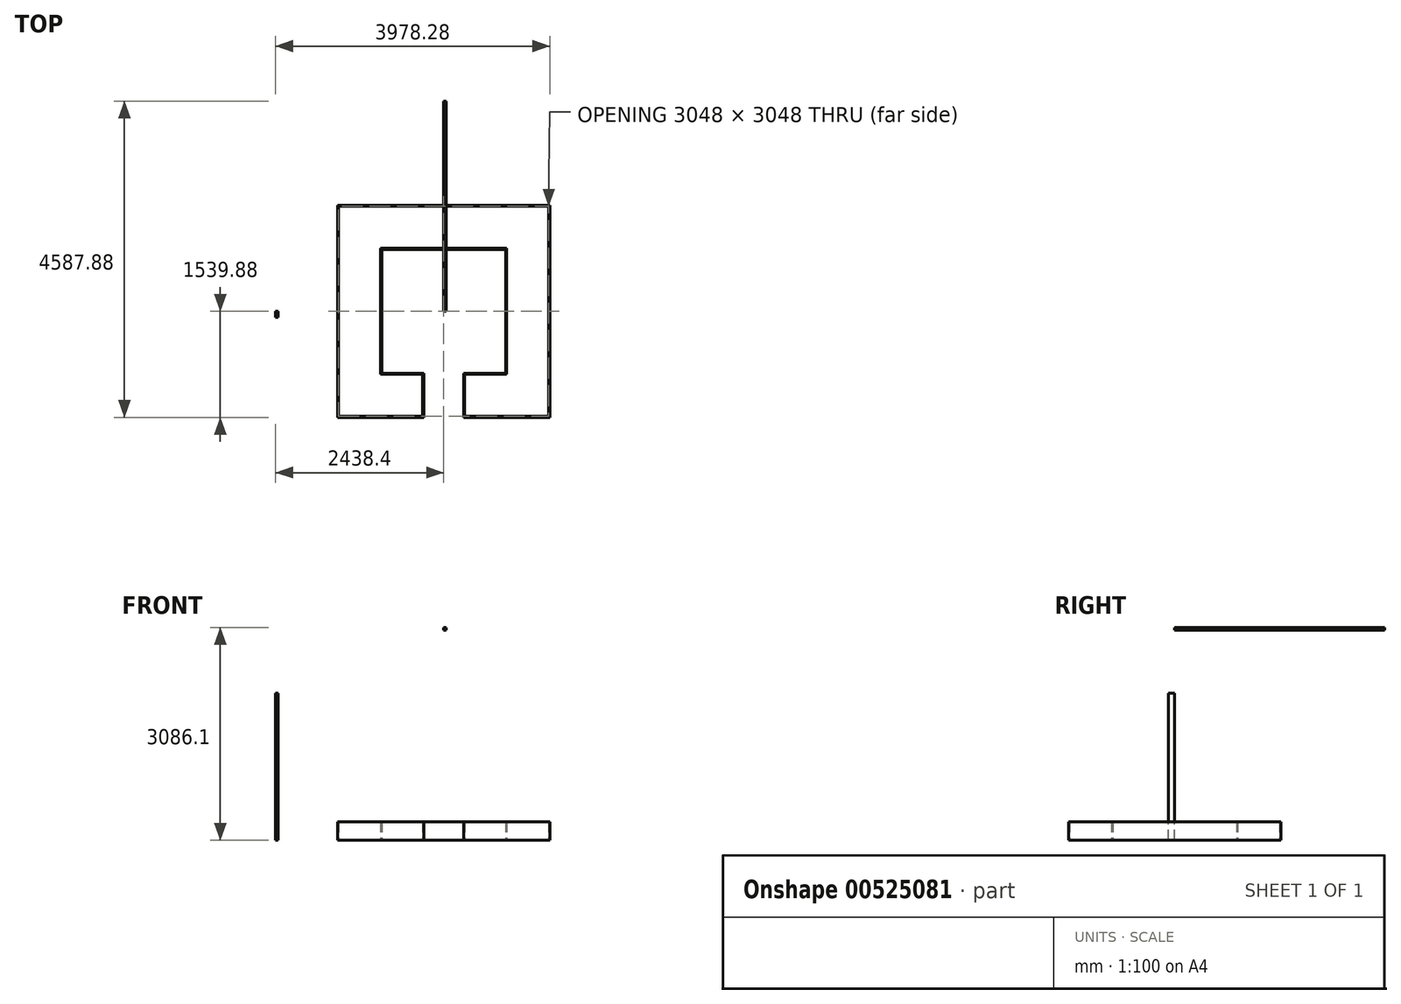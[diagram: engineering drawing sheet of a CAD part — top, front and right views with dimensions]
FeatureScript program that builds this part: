
annotation { "Feature Type Name" : "Feature", "Feature Type Description" : "" }
export const myFeature = defineFeature(function(context is Context, id is Id, definition is map)
    precondition{}
    {
        {
            var Q0;
            Q0=qCreatedBy(makeId("Top.planeOp"),FACE);
            var sketch = newSketch(context, id + "F0", { "sketchPlane" : qUnion([Q0])});
            skLineSegment(sketch, "E0.bottom", {"start": v(1524, -1524) * mm, "end": v(304.8, -1524) * mm});
            skLineSegment(sketch, "E0.top", {"start": v(1524, 1524) * mm, "end": v(-1524, 1524) * mm});
            skLineSegment(sketch, "E0.left", {"start": v(1524, -1524) * mm, "end": v(1524, 1524) * mm});
            skLineSegment(sketch, "E0.right", {"start": v(-1524, -1524) * mm, "end": v(-1524, 1524) * mm});
            skPoint(sketch, "E0.middle", {"position": v(0, 0) * mm});
            skLineSegment(sketch, "E1.bottom", {"start": v(1539.88, -1539.88) * mm, "end": v(288.93, -1539.88) * mm});
            skLineSegment(sketch, "E1.top", {"start": v(1539.88, 1539.88) * mm, "end": v(-1539.88, 1539.88) * mm});
            skLineSegment(sketch, "E1.left", {"start": v(1539.88, -1539.88) * mm, "end": v(1539.88, 1539.88) * mm});
            skLineSegment(sketch, "E1.right", {"start": v(-1539.88, -1539.88) * mm, "end": v(-1539.88, 1539.88) * mm});
            skLineSegment(sketch, "E2.bottom", {"start": v(914.4, -914.4) * mm, "end": v(304.8, -914.4) * mm});
            skLineSegment(sketch, "E2.top", {"start": v(914.4, 914.4) * mm, "end": v(-914.4, 914.4) * mm});
            skLineSegment(sketch, "E2.left", {"start": v(914.4, -914.4) * mm, "end": v(914.4, 914.4) * mm});
            skLineSegment(sketch, "E2.right", {"start": v(-914.4, -914.4) * mm, "end": v(-914.4, 914.4) * mm});
            skLineSegment(sketch, "E3.bottom", {"start": v(898.52, -898.52) * mm, "end": v(288.93, -898.52) * mm});
            skLineSegment(sketch, "E3.top", {"start": v(898.52, 898.52) * mm, "end": v(-898.52, 898.52) * mm});
            skLineSegment(sketch, "E3.left", {"start": v(898.52, -898.52) * mm, "end": v(898.52, 898.52) * mm});
            skLineSegment(sketch, "E3.right", {"start": v(-898.52, -898.52) * mm, "end": v(-898.52, 898.52) * mm});
            skLineSegment(sketch, "E4", {"start": v(288.93, -898.52) * mm, "end": v(288.93, -1539.88) * mm});
            skLineSegment(sketch, "E5", {"start": v(-288.93, -898.52) * mm, "end": v(-288.93, -1539.88) * mm});
            skLineSegment(sketch, "E6", {"start": v(304.8, -914.4) * mm, "end": v(304.8, -1524) * mm});
            skLineSegment(sketch, "E7", {"start": v(-304.8, -914.4) * mm, "end": v(-304.8, -1524) * mm});
            skLineSegment(sketch, "E8.trimOffspring", {"start": v(-288.93, -898.52) * mm, "end": v(-898.52, -898.52) * mm});
            skLineSegment(sketch, "E9.trimOffspring", {"start": v(-304.8, -914.4) * mm, "end": v(-914.4, -914.4) * mm});
            skLineSegment(sketch, "E10.trimOffspring", {"start": v(-288.93, -1539.88) * mm, "end": v(-1539.88, -1539.88) * mm});
            skLineSegment(sketch, "E11.trimOffspring", {"start": v(-304.8, -1524) * mm, "end": v(-1524, -1524) * mm});
            skSolve(sketch);
        }
        {
            var Q0;
            Q0 = qSketchRegion(id + "F0", true);
            extrude(context, id + "F1", {"entities" : qUnion([Q0]), "depth" : 266.7 * mm, "offsetDistance" : 30.48 * mm});
        }
        {
            var Q0;
            Q0=qCreatedBy(makeId("Right.planeOp"),FACE);
            cPlane(context, id + "F2", {"entities" : qUnion([Q0]), "cplaneType" : CPlaneType.OFFSET, "offset" : 2438.4 * mm, "oppositeDirection" : true, "width" : 152.4 * mm, "height" : 152.4 * mm});
        }
        {
            var Q0;
            Q0=qCreatedBy(id+"F2.planeOp",FACE);
            var sketch = newSketch(context, id + "F3", { "sketchPlane" : qUnion([Q0])});
            skLineSegment(sketch, "E12.bottom", {"start": v(0, 0) * mm, "end": v(-88.9, 0) * mm});
            skLineSegment(sketch, "E12.top", {"start": v(0, 2133.6) * mm, "end": v(-88.9, 2133.6) * mm});
            skLineSegment(sketch, "E12.left", {"start": v(0, 0) * mm, "end": v(0, 2133.6) * mm});
            skLineSegment(sketch, "E12.right", {"start": v(-88.9, 0) * mm, "end": v(-88.9, 2133.6) * mm});
            skSolve(sketch);
        }
        {
            var Q0;
            Q0 = qSketchRegion(id + "F3", true);
            extrude(context, id + "F4", {"entities" : qUnion([Q0]), "depth" : 38.1 * mm, "offsetDistance" : 30.48 * mm});
        }
        {
            var Q0;
            Q0=qCreatedBy(makeId("Top.planeOp"),FACE);
            cPlane(context, id + "F5", {"entities" : qUnion([Q0]), "cplaneType" : CPlaneType.OFFSET, "offset" : 3048 * mm, "width" : 152.4 * mm, "height" : 152.4 * mm});
        }
        {
            var Q0;
            Q0=qCreatedBy(id+"F5.planeOp",FACE);
            var sketch = newSketch(context, id + "F6", { "sketchPlane" : qUnion([Q0])});
            skLineSegment(sketch, "E13.bottom", {"start": v(0, 0) * mm, "end": v(38.1, 0) * mm});
            skLineSegment(sketch, "E13.top", {"start": v(0, 3048) * mm, "end": v(38.1, 3048) * mm});
            skLineSegment(sketch, "E13.left", {"start": v(0, 0) * mm, "end": v(0, 3048) * mm});
            skLineSegment(sketch, "E13.right", {"start": v(38.1, 0) * mm, "end": v(38.1, 3048) * mm});
            skSolve(sketch);
        }
        {
            var Q0;
            Q0=makeQuery(id+"F6.imprint","IMPRINT",FACE,{"disambiguationData":[TD([[makeQuery(id+"F6.imprint","IMPRINT",EDGE,{"derivedFrom":sQuery(id+"F6.wireOp",EDGE,"E13.bottom")}),1.0]])]});
            extrude(context, id + "F7", {"entities" : qUnion([Q0]), "depth" : 38.1 * mm, "offsetDistance" : 30.48 * mm});
        }
    });
